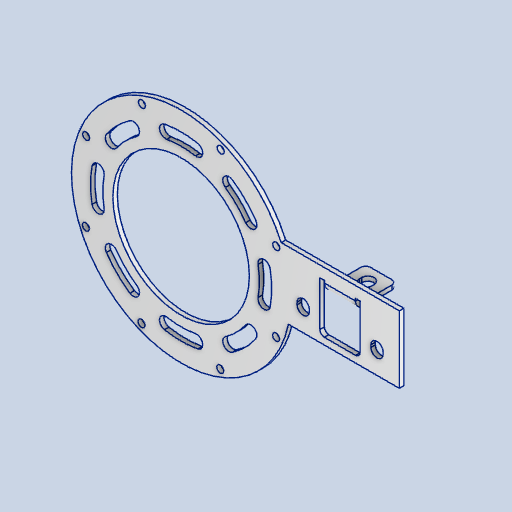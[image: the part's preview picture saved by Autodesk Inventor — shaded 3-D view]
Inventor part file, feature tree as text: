
AUTODESK INVENTOR PART (.ipt)
format: ipt  version: 2023 (Build 270158000, 158)  size: 1,668,608 bytes
history: native  units: mm
features: other x5, extrude x1, fillet x1, sketch x1
ambient origin geometry x8: Origin, YZ Plane, XZ Plane, XY Plane, X Axis, Y Axis, Z Axis, Center Point
bodies: Body1 (feature_tree), Body2 (feature_tree)
feature tree (8):
  other  "GIM8108-8_1.ipt"
  extrude  "押し出し2"  Depth=10.0mm
  other  "折り曲げ3"
  fillet  "フィレット5"  Radius=98.0mm
  other  "TaggingFeature1"
  sketch  "スケッチ17"
  other  "ソリッド1::GIM8108-8_1.ipt"
  other  "Srf1"
